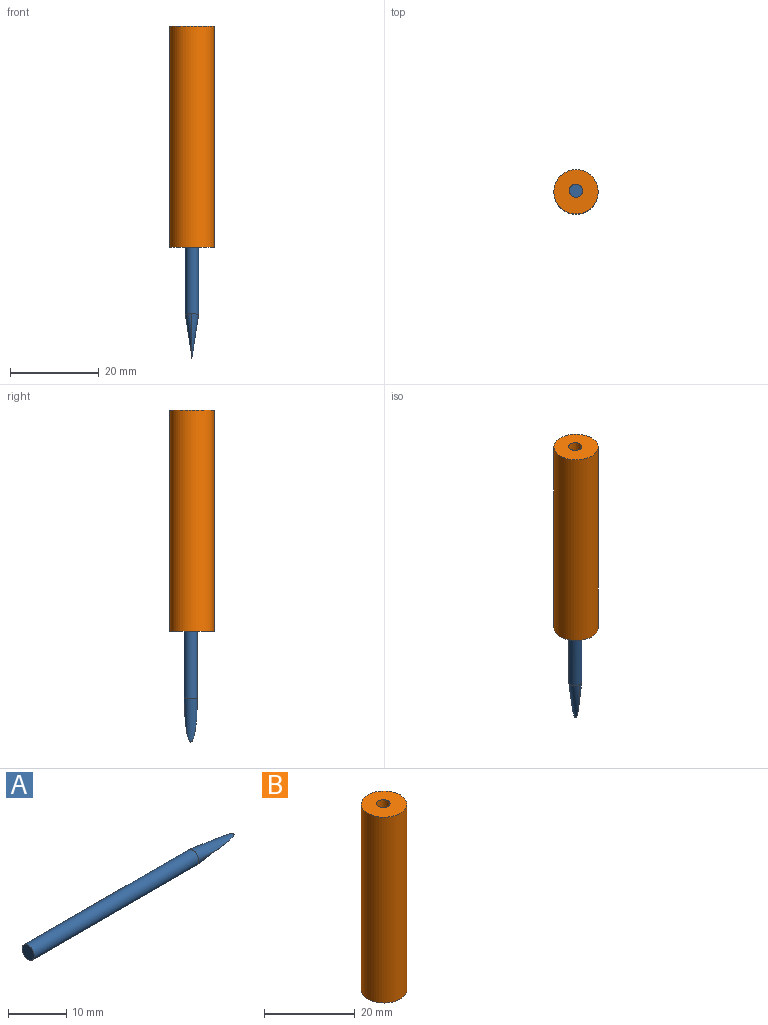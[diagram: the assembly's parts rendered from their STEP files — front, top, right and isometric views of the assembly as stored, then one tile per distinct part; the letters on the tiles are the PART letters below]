
ASSEMBLY  parts=2 mates=1
PART A: 4 faces, bbox 50x3x3 mm
  f0: plane 3x3mm, normal (-1,0,0), area 7.1mm2, adj f1
  f1: cylinder r=1.5mm len=40.11mm, axis (-1,0,0), area 377.7mm2, adj f0,f2,f3
  f2: cylinder r=1.5mm len=10.11mm, axis (-0.99,0,-0.15), area 30mm2, adj f1,f3
  f3: cylinder r=1.5mm len=10.11mm, axis (0.99,0,-0.15), area 30mm2, adj f1,f2
PART B: 4 faces, bbox 10x10x50 mm
  f0: cylinder r=1.5mm len=50mm, axis (0,0,-1), area 471.2mm2, adj f2,f3
  f1: cylinder r=5mm len=50mm, axis (0,0,-1), area 1570.8mm2, adj f2,f3
  f2: plane 10x10mm, normal (0,0,1), area 71.5mm2, adj f0,f1
  f3: plane 10x10mm, normal (0,0,-1), area 71.5mm2, adj f0,f1
PLACE A rot(axis=(0,1,0),90deg) t=(-20.11,-0.09,-21.92)mm
PLACE B t=(-21.61,-0.09,-6.81)mm
MATE cylindrical A.f1 <-> B.f0  axis (0,0,1) through (-21.61,-0.09,18.19)mm
